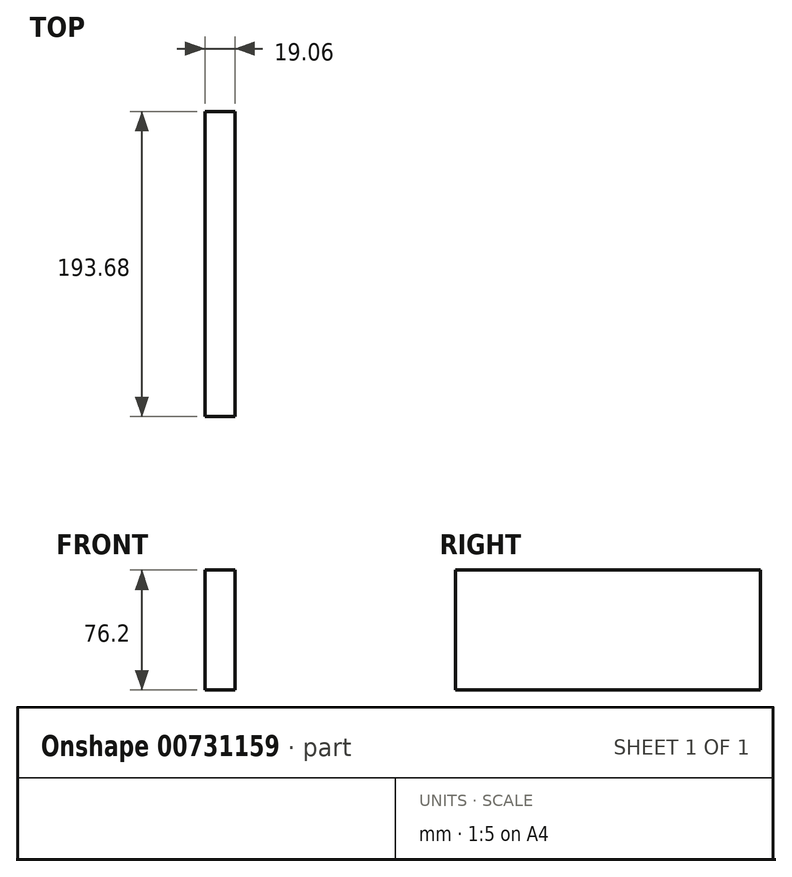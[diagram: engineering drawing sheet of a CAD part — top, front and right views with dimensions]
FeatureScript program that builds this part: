
annotation { "Feature Type Name" : "Feature", "Feature Type Description" : "" }
export const myFeature = defineFeature(function(context is Context, id is Id, definition is map)
    precondition{}
    {
        {
            var Q0;
            Q0=qCreatedBy(makeId("Front.planeOp"),FACE);
            var sketch = newSketch(context, id + "F0", { "sketchPlane" : qUnion([Q0])});
            skLineSegment(sketch, "E0.bottom", {"start": v(-9.52, -38.1) * mm, "end": v(9.53, -38.1) * mm});
            skLineSegment(sketch, "E0.top", {"start": v(-9.53, 38.1) * mm, "end": v(9.52, 38.1) * mm});
            skLineSegment(sketch, "E0.left", {"start": v(-9.52, -38.1) * mm, "end": v(-9.53, 38.1) * mm});
            skLineSegment(sketch, "E0.right", {"start": v(9.53, -38.1) * mm, "end": v(9.53, 38.1) * mm});
            skPoint(sketch, "E0.middle", {"position": v(0, 0) * mm});
            skSolve(sketch);
        }
        {
            var Q0;
            Q0 = qSketchRegion(id + "F0", true);
            extrude(context, id + "F1", {"entities" : qUnion([Q0]), "endBound" : BoundingType.SYMMETRIC, "depth" : 193.67 * mm, "offsetDistance" : 25.4 * mm});
        }
    });
